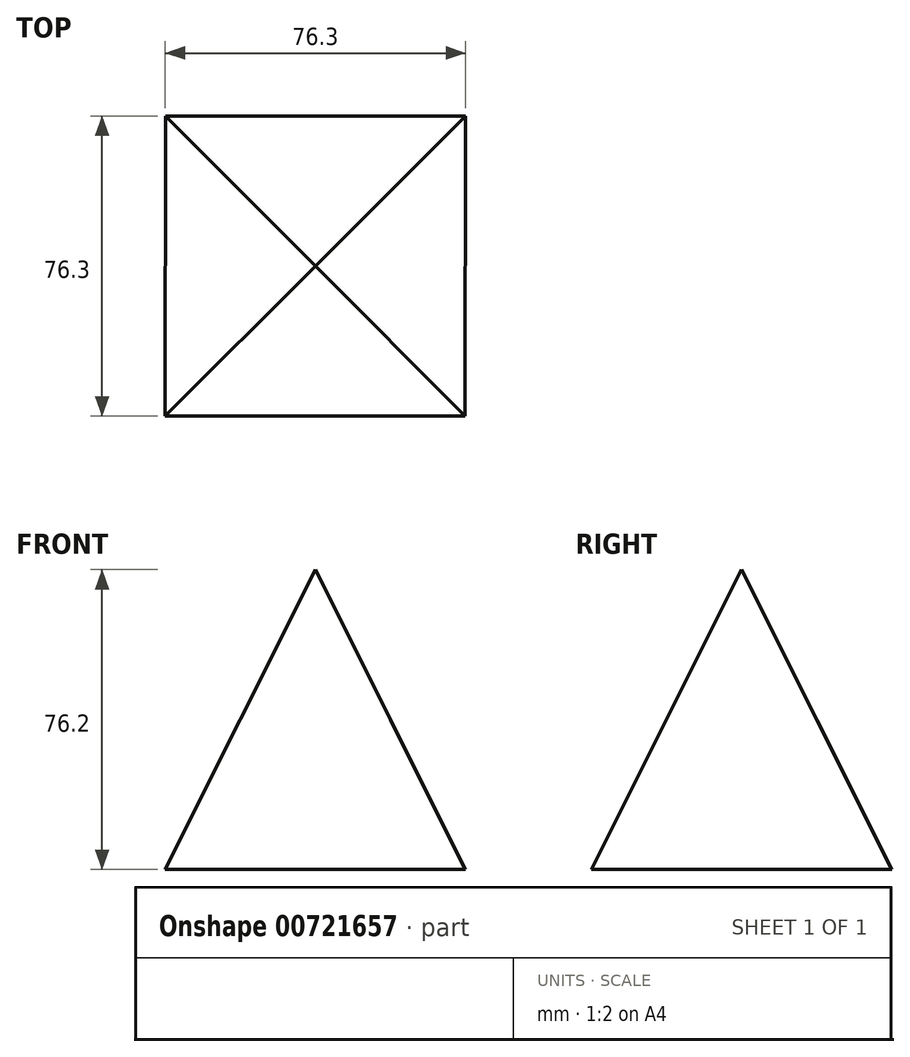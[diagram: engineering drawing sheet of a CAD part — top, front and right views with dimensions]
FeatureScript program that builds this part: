
annotation { "Feature Type Name" : "Feature", "Feature Type Description" : "" }
export const myFeature = defineFeature(function(context is Context, id is Id, definition is map)
    precondition{}
    {
        {
            var Q0;
            Q0=qCreatedBy(makeId("Top.planeOp"),FACE);
            var sketch = newSketch(context, id + "F0", { "sketchPlane" : qUnion([Q0])});
            skCircle(sketch, "E0.cCircle", {"center": v(0, 0) * mm, "radius": 38.1 * mm, "construction": true});
            skLineSegment(sketch, "E0.0", {"start": v(-38.05, 38.15) * mm, "end": v(38.15, 38.05) * mm});
            skLineSegment(sketch, "E0.1", {"start": v(38.15, 38.05) * mm, "end": v(38.05, -38.15) * mm});
            skLineSegment(sketch, "E0.2", {"start": v(38.05, -38.15) * mm, "end": v(-38.15, -38.05) * mm});
            skLineSegment(sketch, "E0.3", {"start": v(-38.15, -38.05) * mm, "end": v(-38.05, 38.15) * mm});
            skPoint(sketch, "E0.0.midPoint", {"position": v(0.05, 38.1) * mm});
            skSolve(sketch);
        }
        {
            var Q0;
            Q0=qCreatedBy(makeId("Top.planeOp"),FACE);
            cPlane(context, id + "F1", {"entities" : qUnion([Q0]), "cplaneType" : CPlaneType.OFFSET, "offset" : 76.2 * mm, "width" : 152.4 * mm, "height" : 152.4 * mm});
        }
        {
            var Q0;
            Q0=qCreatedBy(id+"F1.planeOp",FACE);
            var sketch = newSketch(context, id + "F2", { "sketchPlane" : qUnion([Q0])});
            skPoint(sketch, "E1", {"position": v(0, 0) * mm});
            skSolve(sketch);
        }
        {
            var Q0;
            Q0=makeQuery(id+"F0.imprint","IMPRINT",FACE,{"disambiguationData":[TD([[makeQuery(id+"F0.imprint","IMPRINT",EDGE,{"derivedFrom":sQuery(id+"F0.wireOp",EDGE,"E0.0")}),-1.0]])]});
            var Q1;
            Q1=sQuery(id+"F2.wireOp",VERTEX,"E1");
            loft(context, id + "F3", {"sheetProfilesArray" : [{ "sheetProfileEntities" : qUnion([Q0]) }, { "sheetProfileEntities" : qUnion([Q1]) }]});
        }
    });
